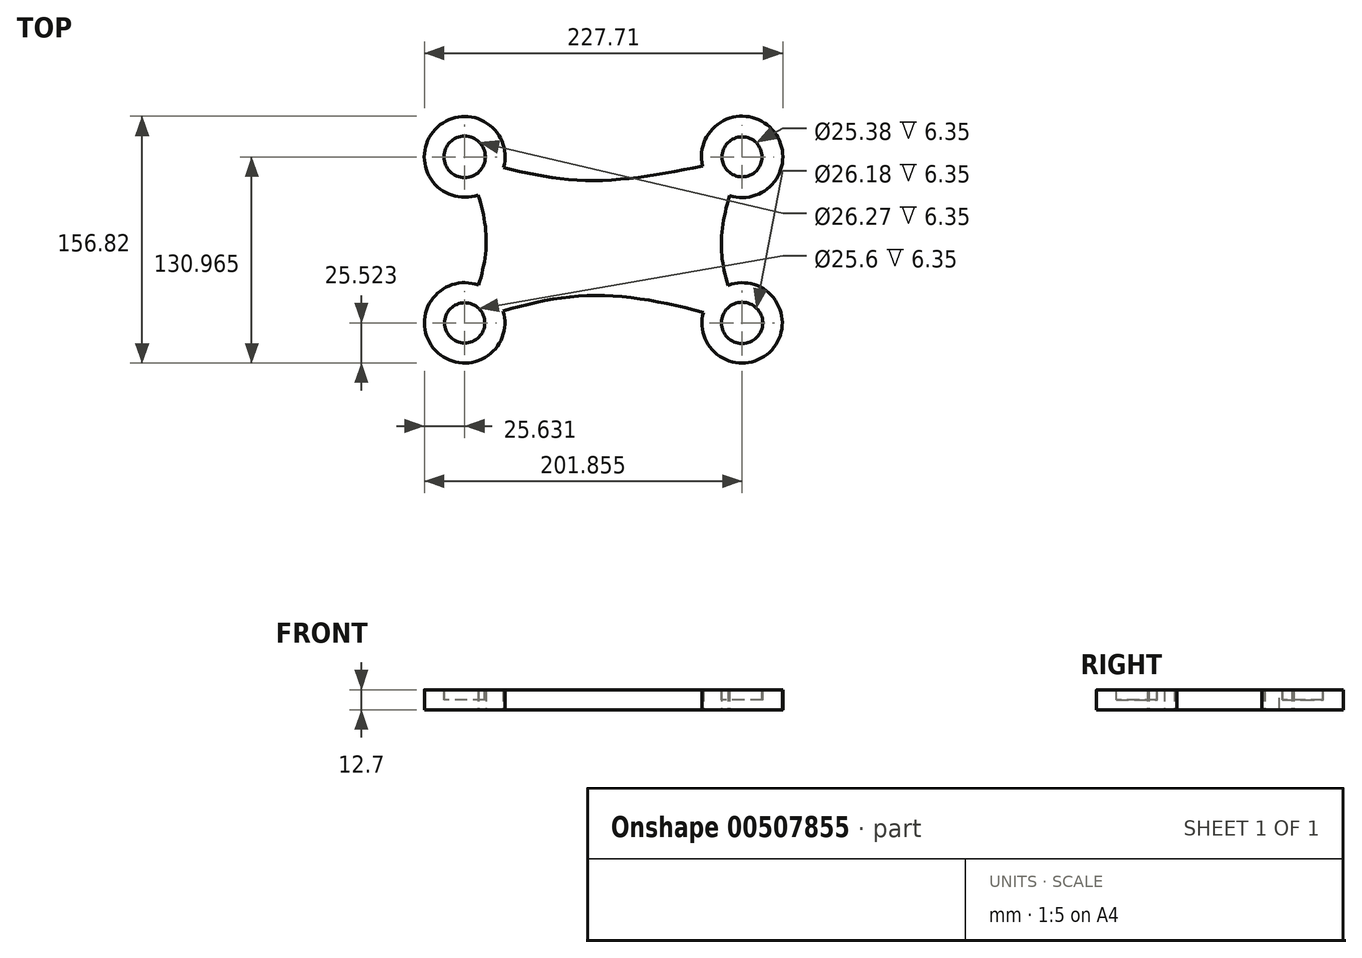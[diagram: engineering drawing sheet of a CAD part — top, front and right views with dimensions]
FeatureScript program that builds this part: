
annotation { "Feature Type Name" : "Feature", "Feature Type Description" : "" }
export const myFeature = defineFeature(function(context is Context, id is Id, definition is map)
    precondition{}
    {
        {
            var Q0;
            Q0=qCreatedBy(makeId("Top.planeOp"),FACE);
            var sketch = newSketch(context, id + "F0", { "sketchPlane" : qUnion([Q0])});
            skLineSegment(sketch, "E0.bottom", {"start": v(-97.98, -48.13) * mm, "end": v(78.25, -48.13) * mm});
            skLineSegment(sketch, "E0.top", {"start": v(-97.98, 57.32) * mm, "end": v(78.25, 57.32) * mm});
            skLineSegment(sketch, "E0.left", {"start": v(-97.98, -48.13) * mm, "end": v(-97.98, 57.32) * mm});
            skLineSegment(sketch, "E0.right", {"start": v(78.25, -48.13) * mm, "end": v(78.25, 57.32) * mm});
            skFitSpline(sketch, "E1", {"points": [v(-97.98, 57.32) * mm, v(-84.27, 3.64) * mm, v(-97.98, -48.13) * mm], "startDerivative": vector(41.01, -106.97) * mm, "endDerivative": vector(-41.25, -103.91) * mm});
            skFitSpline(sketch, "E2", {"points": [v(-97.98, -48.13) * mm, v(-16.58, -30.66) * mm, v(78.25, -48.13) * mm], "startDerivative": vector(165.65, 53.12) * mm, "endDerivative": vector(186.55, -51.83) * mm});
            skFitSpline(sketch, "E3", {"points": [v(78.25, -48.13) * mm, v(65.05, 0) * mm, v(78.25, 57.32) * mm], "startDerivative": vector(-40.2, 98.04) * mm, "endDerivative": vector(39.12, 112.64) * mm});
            skFitSpline(sketch, "E4", {"points": [v(-97.98, 57.32) * mm, v(-19.7, 42.33) * mm, v(78.25, 57.32) * mm], "startDerivative": vector(160.78, -45.9) * mm, "endDerivative": vector(191.12, 44.27) * mm});
            skCircle(sketch, "E5", {"center": v(-97.98, -48.13) * mm, "radius": 25.52 * mm});
            skCircle(sketch, "E6", {"center": v(78.25, -48.13) * mm, "radius": 25.5 * mm});
            skCircle(sketch, "E7", {"center": v(78.25, 57.32) * mm, "radius": 25.85 * mm});
            skCircle(sketch, "E8", {"center": v(-97.98, 57.32) * mm, "radius": 25.63 * mm});
            skSolve(sketch);
        }
        {
            var Q0;
            {var subQ1=sQuery(id+"F0.wireOp",EDGE,"E1");var subQ3=sQuery(id+"F0.wireOp",EDGE,"E8");var subQ4=makeQuery(id+"F0.imprint","INTERSECT",VERTEX,{"derivedFrom":[subQ1,subQ3]});Q0=makeQuery(id+"F0.imprint","IMPRINT",FACE,{"disambiguationData":[TD([[makeQuery(id+"F0.imprint","IMPRINT",EDGE,{"disambiguationData":[TD([[subQ4,-1.0]])],"derivedFrom":subQ3}),1.0]])]});}
            var Q1;
            {var subQ1=sQuery(id+"F0.wireOp",EDGE,"E0.top");var subQ3=sQuery(id+"F0.wireOp",EDGE,"E8");var subQ4=makeQuery(id+"F0.imprint","INTERSECT",VERTEX,{"derivedFrom":[subQ1,subQ3]});Q1=makeQuery(id+"F0.imprint","IMPRINT",FACE,{"disambiguationData":[TD([[makeQuery(id+"F0.imprint","IMPRINT",EDGE,{"disambiguationData":[TD([[subQ4,1.0]])],"derivedFrom":subQ3}),1.0]])]});}
            var Q2;
            {var subQ1=sQuery(id+"F0.wireOp",EDGE,"E0.left");var subQ3=sQuery(id+"F0.wireOp",EDGE,"E8");var subQ4=makeQuery(id+"F0.imprint","INTERSECT",VERTEX,{"derivedFrom":[subQ1,subQ3]});Q2=makeQuery(id+"F0.imprint","IMPRINT",FACE,{"disambiguationData":[TD([[makeQuery(id+"F0.imprint","IMPRINT",EDGE,{"disambiguationData":[TD([[subQ4,-1.0]])],"derivedFrom":subQ3}),1.0]])]});}
            var Q3;
            {var subQ1=sQuery(id+"F0.wireOp",EDGE,"E0.top");var subQ3=sQuery(id+"F0.wireOp",EDGE,"E8");var subQ4=makeQuery(id+"F0.imprint","INTERSECT",VERTEX,{"derivedFrom":[subQ1,subQ3]});Q3=makeQuery(id+"F0.imprint","IMPRINT",FACE,{"disambiguationData":[TD([[makeQuery(id+"F0.imprint","IMPRINT",EDGE,{"disambiguationData":[TD([[subQ4,-1.0]])],"derivedFrom":subQ3}),1.0]])]});}
            var Q4;
            {var subQ1=sQuery(id+"F0.wireOp",EDGE,"E0.left");var subQ3=sQuery(id+"F0.wireOp",EDGE,"E5");var subQ4=makeQuery(id+"F0.imprint","INTERSECT",VERTEX,{"derivedFrom":[subQ1,subQ3]});Q4=makeQuery(id+"F0.imprint","IMPRINT",FACE,{"disambiguationData":[TD([[makeQuery(id+"F0.imprint","IMPRINT",EDGE,{"disambiguationData":[TD([[subQ4,1.0]])],"derivedFrom":subQ3}),1.0]])]});}
            var Q5;
            {var subQ1=sQuery(id+"F0.wireOp",EDGE,"E0.bottom");var subQ3=sQuery(id+"F0.wireOp",EDGE,"E5");var subQ4=makeQuery(id+"F0.imprint","INTERSECT",VERTEX,{"derivedFrom":[subQ1,subQ3]});Q5=makeQuery(id+"F0.imprint","IMPRINT",FACE,{"disambiguationData":[TD([[makeQuery(id+"F0.imprint","IMPRINT",EDGE,{"disambiguationData":[TD([[subQ4,-1.0]])],"derivedFrom":subQ3}),1.0]])]});}
            var Q6;
            {var subQ1=sQuery(id+"F0.wireOp",EDGE,"E1");var subQ3=sQuery(id+"F0.wireOp",EDGE,"E5");var subQ4=makeQuery(id+"F0.imprint","INTERSECT",VERTEX,{"derivedFrom":[subQ1,subQ3]});Q6=makeQuery(id+"F0.imprint","IMPRINT",FACE,{"disambiguationData":[TD([[makeQuery(id+"F0.imprint","IMPRINT",EDGE,{"disambiguationData":[TD([[subQ4,1.0]])],"derivedFrom":subQ3}),1.0]])]});}
            var Q7;
            {var subQ1=sQuery(id+"F0.wireOp",EDGE,"E0.bottom");var subQ3=sQuery(id+"F0.wireOp",EDGE,"E5");var subQ4=makeQuery(id+"F0.imprint","INTERSECT",VERTEX,{"derivedFrom":[subQ1,subQ3]});Q7=makeQuery(id+"F0.imprint","IMPRINT",FACE,{"disambiguationData":[TD([[makeQuery(id+"F0.imprint","IMPRINT",EDGE,{"disambiguationData":[TD([[subQ4,1.0]])],"derivedFrom":subQ3}),1.0]])]});}
            var Q8;
            {var subQ1=sQuery(id+"F0.wireOp",EDGE,"E2");var subQ3=sQuery(id+"F0.wireOp",EDGE,"E6");var subQ4=makeQuery(id+"F0.imprint","INTERSECT",VERTEX,{"derivedFrom":[subQ1,subQ3]});Q8=makeQuery(id+"F0.imprint","IMPRINT",FACE,{"disambiguationData":[TD([[makeQuery(id+"F0.imprint","IMPRINT",EDGE,{"disambiguationData":[TD([[subQ4,1.0]])],"derivedFrom":subQ3}),1.0]])]});}
            var Q9;
            {var subQ1=sQuery(id+"F0.wireOp",EDGE,"E0.right");var subQ3=sQuery(id+"F0.wireOp",EDGE,"E6");var subQ4=makeQuery(id+"F0.imprint","INTERSECT",VERTEX,{"derivedFrom":[subQ1,subQ3]});Q9=makeQuery(id+"F0.imprint","IMPRINT",FACE,{"disambiguationData":[TD([[makeQuery(id+"F0.imprint","IMPRINT",EDGE,{"disambiguationData":[TD([[subQ4,-1.0]])],"derivedFrom":subQ3}),1.0]])]});}
            var Q10;
            {var subQ1=sQuery(id+"F0.wireOp",EDGE,"E0.bottom");var subQ3=sQuery(id+"F0.wireOp",EDGE,"E6");var subQ4=makeQuery(id+"F0.imprint","INTERSECT",VERTEX,{"derivedFrom":[subQ1,subQ3]});Q10=makeQuery(id+"F0.imprint","IMPRINT",FACE,{"disambiguationData":[TD([[makeQuery(id+"F0.imprint","IMPRINT",EDGE,{"disambiguationData":[TD([[subQ4,1.0]])],"derivedFrom":subQ3}),1.0]])]});}
            var Q11;
            {var subQ1=sQuery(id+"F0.wireOp",EDGE,"E0.bottom");var subQ3=sQuery(id+"F0.wireOp",EDGE,"E6");var subQ4=makeQuery(id+"F0.imprint","INTERSECT",VERTEX,{"derivedFrom":[subQ1,subQ3]});Q11=makeQuery(id+"F0.imprint","IMPRINT",FACE,{"disambiguationData":[TD([[makeQuery(id+"F0.imprint","IMPRINT",EDGE,{"disambiguationData":[TD([[subQ4,-1.0]])],"derivedFrom":subQ3}),1.0]])]});}
            var Q12;
            {var subQ1=sQuery(id+"F0.wireOp",EDGE,"E0.right");var subQ3=sQuery(id+"F0.wireOp",EDGE,"E7");var subQ4=makeQuery(id+"F0.imprint","INTERSECT",VERTEX,{"derivedFrom":[subQ1,subQ3]});Q12=makeQuery(id+"F0.imprint","IMPRINT",FACE,{"disambiguationData":[TD([[makeQuery(id+"F0.imprint","IMPRINT",EDGE,{"disambiguationData":[TD([[subQ4,1.0]])],"derivedFrom":subQ3}),1.0]])]});}
            var Q13;
            {var subQ1=sQuery(id+"F0.wireOp",EDGE,"E3");var subQ3=sQuery(id+"F0.wireOp",EDGE,"E7");var subQ4=makeQuery(id+"F0.imprint","INTERSECT",VERTEX,{"derivedFrom":[subQ1,subQ3]});Q13=makeQuery(id+"F0.imprint","IMPRINT",FACE,{"disambiguationData":[TD([[makeQuery(id+"F0.imprint","IMPRINT",EDGE,{"disambiguationData":[TD([[subQ4,1.0]])],"derivedFrom":subQ3}),1.0]])]});}
            var Q14;
            {var subQ1=sQuery(id+"F0.wireOp",EDGE,"E0.top");var subQ3=sQuery(id+"F0.wireOp",EDGE,"E7");var subQ4=makeQuery(id+"F0.imprint","INTERSECT",VERTEX,{"derivedFrom":[subQ1,subQ3]});Q14=makeQuery(id+"F0.imprint","IMPRINT",FACE,{"disambiguationData":[TD([[makeQuery(id+"F0.imprint","IMPRINT",EDGE,{"disambiguationData":[TD([[subQ4,-1.0]])],"derivedFrom":subQ3}),1.0]])]});}
            var Q15;
            {var subQ1=sQuery(id+"F0.wireOp",EDGE,"E0.top");var subQ3=sQuery(id+"F0.wireOp",EDGE,"E7");var subQ4=makeQuery(id+"F0.imprint","INTERSECT",VERTEX,{"derivedFrom":[subQ1,subQ3]});Q15=makeQuery(id+"F0.imprint","IMPRINT",FACE,{"disambiguationData":[TD([[makeQuery(id+"F0.imprint","IMPRINT",EDGE,{"disambiguationData":[TD([[subQ4,1.0]])],"derivedFrom":subQ3}),1.0]])]});}
            var Q16;
            {var subQ0=sQuery(id+"F0.wireOp",EDGE,"E8");var subQ13=sQuery(id+"F0.wireOp",EDGE,"E1");var subQ14=makeQuery(id+"F0.imprint","INTERSECT",VERTEX,{"derivedFrom":[subQ13,subQ0]});Q16=makeQuery(id+"F0.imprint","IMPRINT",FACE,{"disambiguationData":[TD([[makeQuery(id+"F0.imprint","IMPRINT",EDGE,{"disambiguationData":[TD([[subQ14,-1.0]])],"derivedFrom":subQ13}),1.0]])]});}
            extrude(context, id + "F1", {"entities" : qUnion([Q0, Q1, Q2, Q3, Q4, Q5, Q6, Q7, Q8, Q9, Q10, Q11, Q12, Q13, Q14, Q15, Q16]), "depth" : 12.7 * mm});
        }
        {
            var Q0;
            Q0=makeQuery(id+"F1.opExtrude","CAP_FACE",FACE,{"disambiguationData":[OSD([sQuery(id+"F0.wireOp",EDGE,"E1"),sQuery(id+"F0.wireOp",EDGE,"E2"),sQuery(id+"F0.wireOp",EDGE,"E3"),sQuery(id+"F0.wireOp",EDGE,"E4"),sQuery(id+"F0.wireOp",EDGE,"E5"),sQuery(id+"F0.wireOp",EDGE,"E6"),sQuery(id+"F0.wireOp",EDGE,"E7"),sQuery(id+"F0.wireOp",EDGE,"E8")])],"isStart":false});
            var sketch = newSketch(context, id + "F2", { "sketchPlane" : qUnion([Q0])});
            skCircle(sketch, "E9", {"center": v(78.25, 57.32) * mm, "radius": 12.69 * mm});
            skSolve(sketch);
        }
        {
            var Q0;
            Q0 = qSketchRegion(id + "F2", true);
            extrude(context, id + "F3", {"entities" : qUnion([Q0]), "operationType" : NewBodyOperationType.REMOVE, "oppositeDirection" : true, "depth" : 6.35 * mm});
        }
        {
            var Q0;
            Q0=makeQuery(id+"F1.opExtrude","CAP_FACE",FACE,{"disambiguationData":[OSD([sQuery(id+"F0.wireOp",EDGE,"E1"),sQuery(id+"F0.wireOp",EDGE,"E2"),sQuery(id+"F0.wireOp",EDGE,"E3"),sQuery(id+"F0.wireOp",EDGE,"E4"),sQuery(id+"F0.wireOp",EDGE,"E5"),sQuery(id+"F0.wireOp",EDGE,"E6"),sQuery(id+"F0.wireOp",EDGE,"E7"),sQuery(id+"F0.wireOp",EDGE,"E8")])],"isStart":false});
            var sketch = newSketch(context, id + "F4", { "sketchPlane" : qUnion([Q0])});
            skCircle(sketch, "E10", {"center": v(78.25, -48.13) * mm, "radius": 13.1 * mm});
            skSolve(sketch);
        }
        {
            var Q0;
            Q0=makeQuery(id+"F4.imprint","IMPRINT",FACE,{"disambiguationData":[TD([[makeQuery(id+"F4.imprint","IMPRINT",EDGE,{"derivedFrom":sQuery(id+"F4.wireOp",EDGE,"E10")}),1.0]])]});
            extrude(context, id + "F5", {"entities" : qUnion([Q0]), "operationType" : NewBodyOperationType.REMOVE, "oppositeDirection" : true, "depth" : 6.35 * mm});
        }
        {
            var Q0;
            Q0=makeQuery(id+"F1.opExtrude","CAP_FACE",FACE,{"disambiguationData":[OSD([sQuery(id+"F0.wireOp",EDGE,"E1"),sQuery(id+"F0.wireOp",EDGE,"E2"),sQuery(id+"F0.wireOp",EDGE,"E3"),sQuery(id+"F0.wireOp",EDGE,"E4"),sQuery(id+"F0.wireOp",EDGE,"E5"),sQuery(id+"F0.wireOp",EDGE,"E6"),sQuery(id+"F0.wireOp",EDGE,"E7"),sQuery(id+"F0.wireOp",EDGE,"E8")])],"isStart":false});
            var sketch = newSketch(context, id + "F6", { "sketchPlane" : qUnion([Q0])});
            skCircle(sketch, "E11", {"center": v(-97.98, 57.32) * mm, "radius": 13.13 * mm});
            skSolve(sketch);
        }
        {
            var Q0;
            Q0 = qSketchRegion(id + "F6", true);
            extrude(context, id + "F7", {"entities" : qUnion([Q0]), "operationType" : NewBodyOperationType.REMOVE, "oppositeDirection" : true, "depth" : 6.35 * mm});
        }
        {
            var Q0;
            Q0=makeQuery(id+"F1.opExtrude","CAP_FACE",FACE,{"disambiguationData":[OSD([sQuery(id+"F0.wireOp",EDGE,"E1"),sQuery(id+"F0.wireOp",EDGE,"E2"),sQuery(id+"F0.wireOp",EDGE,"E3"),sQuery(id+"F0.wireOp",EDGE,"E4"),sQuery(id+"F0.wireOp",EDGE,"E5"),sQuery(id+"F0.wireOp",EDGE,"E6"),sQuery(id+"F0.wireOp",EDGE,"E7"),sQuery(id+"F0.wireOp",EDGE,"E8")])],"isStart":false});
            var sketch = newSketch(context, id + "F8", { "sketchPlane" : qUnion([Q0])});
            skCircle(sketch, "E12", {"center": v(-97.98, -48.13) * mm, "radius": 12.8 * mm});
            skSolve(sketch);
        }
        {
            var Q0;
            Q0=makeQuery(id+"F8.imprint","IMPRINT",FACE,{"disambiguationData":[TD([[makeQuery(id+"F8.imprint","IMPRINT",EDGE,{"derivedFrom":sQuery(id+"F8.wireOp",EDGE,"E12")}),1.0]])]});
            extrude(context, id + "F9", {"entities" : qUnion([Q0]), "operationType" : NewBodyOperationType.REMOVE, "oppositeDirection" : true, "depth" : 6.35 * mm});
        }
    });
